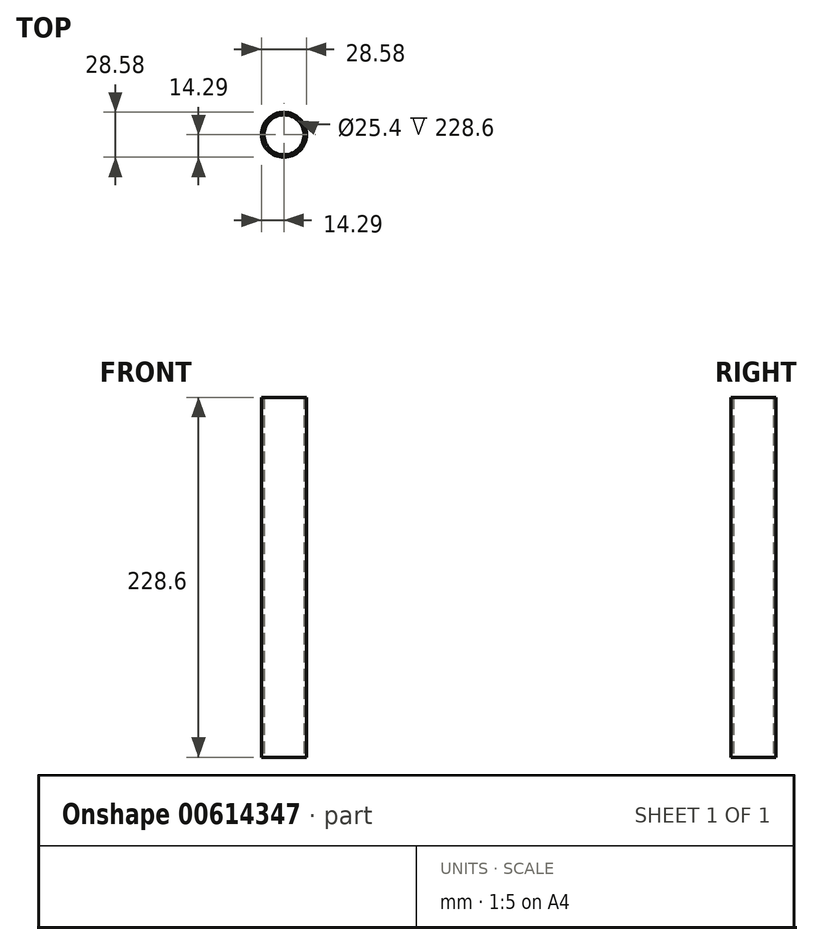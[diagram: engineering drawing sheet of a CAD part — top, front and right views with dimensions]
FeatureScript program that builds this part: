
annotation { "Feature Type Name" : "Feature", "Feature Type Description" : "" }
export const myFeature = defineFeature(function(context is Context, id is Id, definition is map)
    precondition{}
    {
        {
            var Q0;
            Q0=qCreatedBy(makeId("Top.planeOp"),FACE);
            var sketch = newSketch(context, id + "F0", { "sketchPlane" : qUnion([Q0])});
            skLineSegment(sketch, "E0", {"start": v(0, 0) * mm, "end": v(12.7, 0) * mm});
            skCircle(sketch, "E1", {"center": v(0, 0) * mm, "radius": 12.7 * mm});
            skCircle(sketch, "E2.0", {"center": v(0, 0) * mm, "radius": 14.29 * mm});
            skSolve(sketch);
        }
        {
            var Q0;
            Q0=qCreatedBy(makeId("Top.planeOp"),FACE);
            var sketch = newSketch(context, id + "F1", { "sketchPlane" : qUnion([Q0])});
            skSolve(sketch);
        }
        {
            var Q0;
            Q0=qSketchRegion(id+"F1",true);
            var Q1;
            Q1=makeQuery(id+"F0.imprint","IMPRINT",FACE,{"disambiguationData":[TD([[makeQuery(id+"F0.imprint","IMPRINT",EDGE,{"derivedFrom":sQuery(id+"F0.wireOp",EDGE,"E1")}),-1.0]])]});
            extrude(context, id + "F2", {"entities" : qUnion([Q0, Q1]), "depth" : 228.6 * mm, "offsetDistance" : 25.4 * mm});
        }
    });
